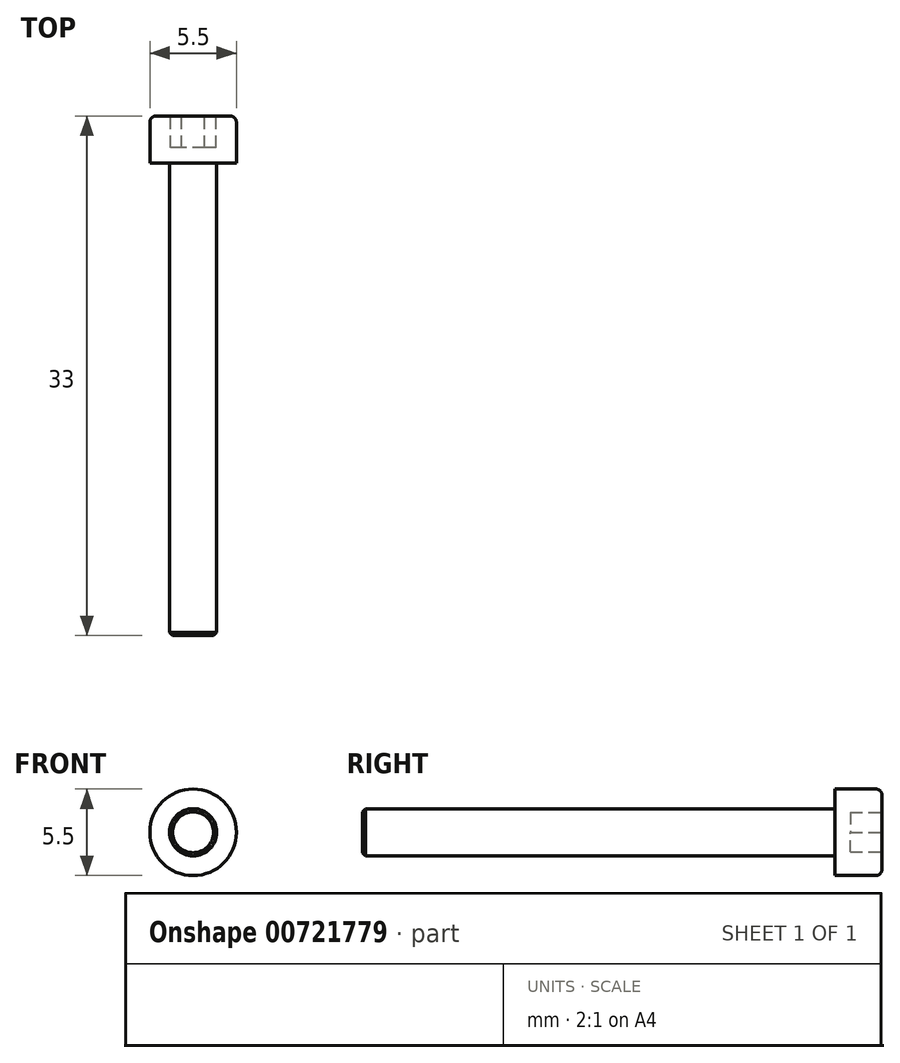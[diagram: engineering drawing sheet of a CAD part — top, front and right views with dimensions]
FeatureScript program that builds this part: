
annotation { "Feature Type Name" : "Feature", "Feature Type Description" : "" }
export const myFeature = defineFeature(function(context is Context, id is Id, definition is map)
    precondition{}
    {
        {
            var Q0;
            Q0=qCreatedBy(makeId("Front.planeOp"),FACE);
            var sketch = newSketch(context, id + "F0", { "sketchPlane" : qUnion([Q0])});
            skCircle(sketch, "E0", {"center": v(0, 0) * mm, "radius": 2.75 * mm});
            skSolve(sketch);
        }
        {
            var Q0;
            Q0=makeQuery(id+"F0.imprint","IMPRINT",FACE,{"disambiguationData":[TD([[makeQuery(id+"F0.imprint","IMPRINT",EDGE,{"derivedFrom":sQuery(id+"F0.wireOp",EDGE,"E0")}),1.0]])]});
            extrude(context, id + "F1", {"entities" : qUnion([Q0]), "depth" : 3 * mm, "offsetDistance" : 25 * mm});
        }
        {
            var Q0;
            Q0=makeQuery(id+"F1.opExtrude","CAP_FACE",FACE,{"disambiguationData":[OSD([sQuery(id+"F0.wireOp",EDGE,"E0")])],"isStart":false});
            var sketch = newSketch(context, id + "F2", { "sketchPlane" : qUnion([Q0])});
            skCircle(sketch, "E1", {"center": v(0, 0) * mm, "radius": 1.5 * mm});
            skSolve(sketch);
        }
        {
            var Q0;
            Q0=makeQuery(id+"F2.imprint","IMPRINT",FACE,{"disambiguationData":[TD([[makeQuery(id+"F2.imprint","IMPRINT",EDGE,{"derivedFrom":sQuery(id+"F2.wireOp",EDGE,"E1")}),1.0]])]});
            extrude(context, id + "F3", {"entities" : qUnion([Q0]), "operationType" : NewBodyOperationType.ADD, "depth" : 30 * mm, "offsetDistance" : 25 * mm});
        }
        {
            var Q0;
            Q0=makeQuery(id+"F3.opExtrude","CAP_EDGE",EDGE,{"disambiguationData":[OSD([sQuery(id+"F2.wireOp",EDGE,"E1")])],"isStart":false});
            chamfer(context, id + "F4", {"entities" : qUnion([Q0]), "width" : 0.2 * mm, "tangentPropagation" : true});
        }
        {
            var Q0;
            Q0=makeQuery(id+"F1.opExtrude","CAP_FACE",FACE,{"disambiguationData":[OSD([sQuery(id+"F0.wireOp",EDGE,"E0")])],"isStart":true});
            var sketch = newSketch(context, id + "F5", { "sketchPlane" : qUnion([Q0])});
            skCircle(sketch, "E2.cCircle", {"center": v(0, 0) * mm, "radius": 1.25 * mm, "construction": true});
            skLineSegment(sketch, "E2.0", {"start": v(0.72, 1.25) * mm, "end": v(1.44, 0) * mm});
            skLineSegment(sketch, "E2.1", {"start": v(1.44, 0) * mm, "end": v(0.72, -1.25) * mm});
            skLineSegment(sketch, "E2.2", {"start": v(0.72, -1.25) * mm, "end": v(-0.72, -1.25) * mm});
            skLineSegment(sketch, "E2.3", {"start": v(-0.72, -1.25) * mm, "end": v(-1.44, 0) * mm});
            skLineSegment(sketch, "E2.4", {"start": v(-1.44, 0) * mm, "end": v(-0.72, 1.25) * mm});
            skLineSegment(sketch, "E2.5", {"start": v(-0.72, 1.25) * mm, "end": v(0.72, 1.25) * mm});
            skPoint(sketch, "E2.0.midPoint", {"position": v(1.08, 0.62) * mm});
            skSolve(sketch);
        }
        {
            var Q0;
            Q0=makeQuery(id+"F5.imprint","IMPRINT",FACE,{"disambiguationData":[TD([[makeQuery(id+"F5.imprint","IMPRINT",EDGE,{"derivedFrom":sQuery(id+"F5.wireOp",EDGE,"E2.0")}),-1.0]])]});
            extrude(context, id + "F6", {"entities" : qUnion([Q0]), "operationType" : NewBodyOperationType.REMOVE, "oppositeDirection" : true, "depth" : 2 * mm, "offsetDistance" : 25 * mm});
        }
        {
            var Q0;
            Q0=makeQuery(id+"F1.opExtrude","CAP_EDGE",EDGE,{"disambiguationData":[OSD([sQuery(id+"F0.wireOp",EDGE,"E0")])],"isStart":true});
            fillet(context, id + "F7", {"entities" : qUnion([Q0]), "radius" : 0.4 * mm, "tangentPropagation" : true, "allowEdgeOverflow" : false});
        }
    });
